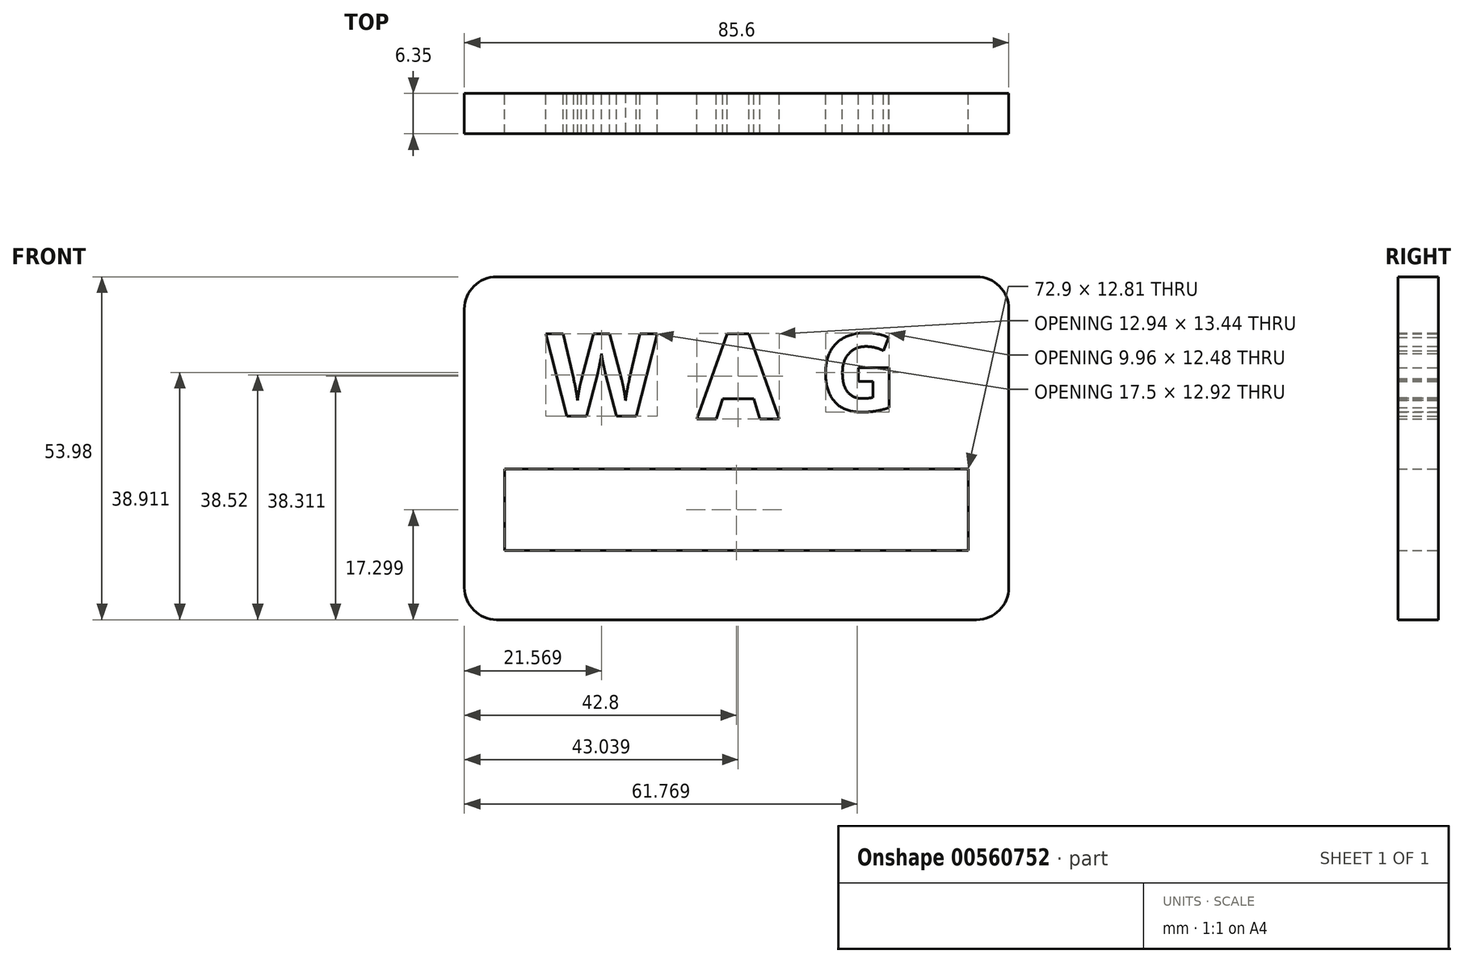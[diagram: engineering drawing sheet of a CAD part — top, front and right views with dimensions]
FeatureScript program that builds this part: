
annotation { "Feature Type Name" : "Feature", "Feature Type Description" : "" }
export const myFeature = defineFeature(function(context is Context, id is Id, definition is map)
    precondition{}
    {
        {
            var Q0;
            Q0=qCreatedBy(makeId("Front.planeOp"),FACE);
            var sketch = newSketch(context, id + "F0", { "sketchPlane" : qUnion([Q0])});
            skLineSegment(sketch, "E0.bottom", {"start": v(-37.72, 26.99) * mm, "end": v(37.72, 26.99) * mm});
            skLineSegment(sketch, "E0.top", {"start": v(-37.72, -26.99) * mm, "end": v(37.72, -26.99) * mm});
            skLineSegment(sketch, "E0.left", {"start": v(-42.8, 21.9) * mm, "end": v(-42.8, -21.9) * mm});
            skLineSegment(sketch, "E0.right", {"start": v(42.8, 21.9) * mm, "end": v(42.8, -21.9) * mm});
            skPoint(sketch, "E0.middle", {"position": v(0, 0) * mm});
            skPoint(sketch, "E1.visualSharp", {"position": v(-42.8, 26.99) * mm});
            skArc(sketch, "E1.filletArc", {"start": v(-37.72, 26.99) * mm, "mid": v(-41.31, 25.5) * mm, "end": v(-42.8, 21.9) * mm});
            skPoint(sketch, "E2.visualSharp", {"position": v(42.8, 26.99) * mm});
            skArc(sketch, "E2.filletArc", {"start": v(42.8, 21.9) * mm, "mid": v(41.31, 25.5) * mm, "end": v(37.72, 26.99) * mm});
            skPoint(sketch, "E3.visualSharp", {"position": v(-42.8, -26.99) * mm});
            skArc(sketch, "E3.filletArc", {"start": v(-42.8, -21.9) * mm, "mid": v(-41.31, -25.5) * mm, "end": v(-37.72, -26.99) * mm});
            skPoint(sketch, "E4.visualSharp", {"position": v(42.8, -26.99) * mm});
            skArc(sketch, "E4.filletArc", {"start": v(37.72, -26.99) * mm, "mid": v(41.31, -25.5) * mm, "end": v(42.8, -21.9) * mm});
            skLineSegment(sketch, "E5.bottom", {"start": v(-36.45, -16.1) * mm, "end": v(36.45, -16.1) * mm});
            skLineSegment(sketch, "E5.top", {"start": v(-36.45, -3.29) * mm, "end": v(36.45, -3.29) * mm});
            skLineSegment(sketch, "E5.left", {"start": v(-36.45, -16.1) * mm, "end": v(-36.45, -3.29) * mm});
            skLineSegment(sketch, "E5.right", {"start": v(36.45, -16.1) * mm, "end": v(36.45, -3.29) * mm});
            skPoint(sketch, "E5.middle", {"position": v(0, -9.7) * mm});
            skText(sketch, "E6", { "text": "A", "fontName": "OpenSans-Bold.ttf"});
            skText(sketch, "E7", { "text": "W", "fontName": "OpenSans-Bold.ttf"});
            skText(sketch, "E8", { "text": "G", "fontName": "OpenSans-Bold.ttf"});
            const initialGuessF0  = {"E6": [-0.00623, 0.0046, 1, 0, 0.0135], "E7": [-0.02998, 0.00507, 1, 0, 0.01303], "E8": [0.013, 0.00585, 1, 0, 0.01224]};
            skSetInitialGuess(sketch, initialGuessF0);
            skSolve(sketch);
        }
        {
            var Q0;
            Q0=makeQuery(id+"F0.imprint","IMPRINT",FACE,{"disambiguationData":[TD([[makeQuery(id+"F0.imprint","IMPRINT",EDGE,{"derivedFrom":sQuery(id+"F0.wireOp",EDGE,"E0.bottom")}),-1.0]])]});
            extrude(context, id + "F1", {"entities" : qUnion([Q0]), "depth" : 2.54 * mm, "offsetDistance" : 25.4 * mm});
        }
        {
            var Q0;
            Q0 = qSketchRegion(id + "F0", true);
            extrude(context, id + "F2", {"entities" : qUnion([Q0]), "operationType" : NewBodyOperationType.ADD, "depth" : 6.35 * mm, "offsetDistance" : 25.4 * mm});
        }
    });
